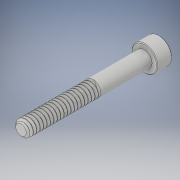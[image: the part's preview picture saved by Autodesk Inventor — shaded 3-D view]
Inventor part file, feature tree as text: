
AUTODESK INVENTOR PART (.ipt)
format: ipt  version: 2018 (Build 220112000, 112)  size: 752,640 bytes
history: native  units: in
note: dims shown in document units (in); Inventor stores cm internally (conversion verified against a paired STEP export)
features: chamfer x1
ambient origin geometry x8: Origin, YZ Plane, XZ Plane, XY Plane, X Axis, Y Axis, Z Axis, Center Point
bodies: Solid1 (feature_tree)
feature tree (1):
  chamfer  "Chamfer2"  [1 undecoded]
note: 1 required parameter value undecoded (feature->parameter linkage not recoverable at this tier; creation-order binding heuristic only, values carry confidence <= 0.55)
